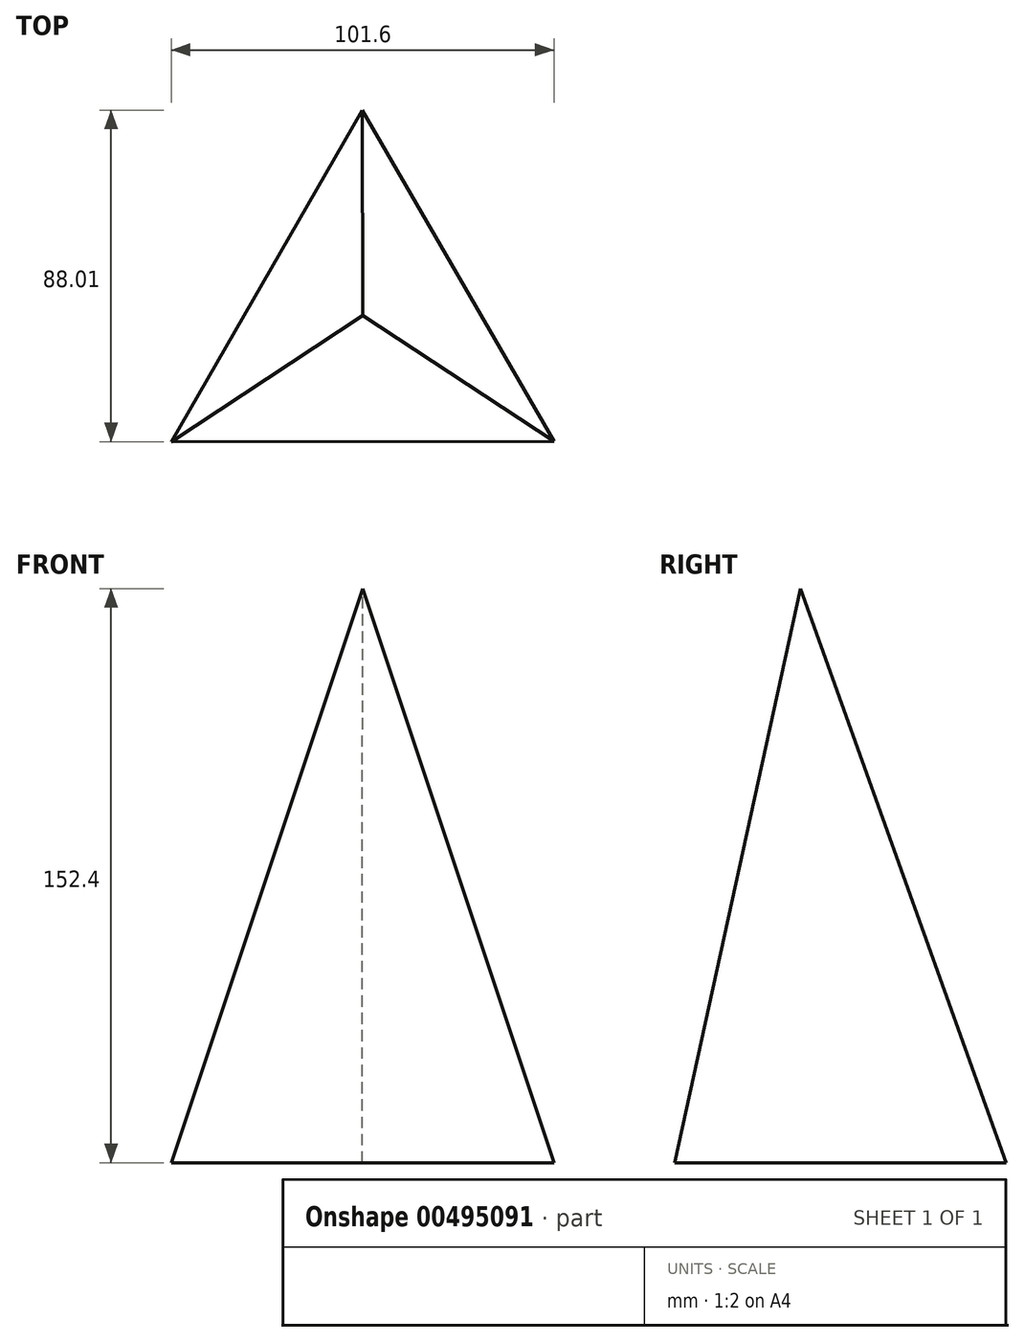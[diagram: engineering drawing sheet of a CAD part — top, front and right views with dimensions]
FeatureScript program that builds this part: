
annotation { "Feature Type Name" : "Feature", "Feature Type Description" : "" }
export const myFeature = defineFeature(function(context is Context, id is Id, definition is map)
    precondition{}
    {
        {
            var Q0;
            Q0=qCreatedBy(makeId("Top.planeOp"),FACE);
            var sketch = newSketch(context, id + "F0", { "sketchPlane" : qUnion([Q0])});
            skCircle(sketch, "E0.cCircle", {"center": v(0, -4.1) * mm, "radius": 58.66 * mm, "construction": true});
            skLineSegment(sketch, "E0.0", {"start": v(-50.78, -33.45) * mm, "end": v(-0.03, 54.56) * mm});
            skLineSegment(sketch, "E0.1", {"start": v(-0.03, 54.56) * mm, "end": v(50.82, -33.4) * mm});
            skLineSegment(sketch, "E0.2", {"start": v(50.82, -33.4) * mm, "end": v(-50.78, -33.45) * mm});
            skSolve(sketch);
        }
        {
            var Q0;
            Q0=qCreatedBy(makeId("Top.planeOp"),FACE);
            cPlane(context, id + "F1", {"entities" : qUnion([Q0]), "cplaneType" : CPlaneType.OFFSET, "offset" : 152.4 * mm, "width" : 152.4 * mm, "height" : 152.4 * mm});
        }
        {
            var Q0;
            Q0=qCreatedBy(id+"F1.planeOp",FACE);
            var sketch = newSketch(context, id + "F2", { "sketchPlane" : qUnion([Q0])});
            skPoint(sketch, "E1", {"position": v(0, 0) * mm});
            skSolve(sketch);
        }
        {
            var Q0;
            Q0=makeQuery(id+"F0.imprint","IMPRINT",FACE,{"disambiguationData":[TD([[makeQuery(id+"F0.imprint","IMPRINT",EDGE,{"derivedFrom":sQuery(id+"F0.wireOp",EDGE,"E0.0")}),-1.0]])]});
            var Q1;
            Q1=sQuery(id+"F2.wireOp",VERTEX,"E1");
            loft(context, id + "F3", {"sheetProfilesArray" : [{ "sheetProfileEntities" : qUnion([Q0]) }, { "sheetProfileEntities" : qUnion([Q1]) }]});
        }
    });
